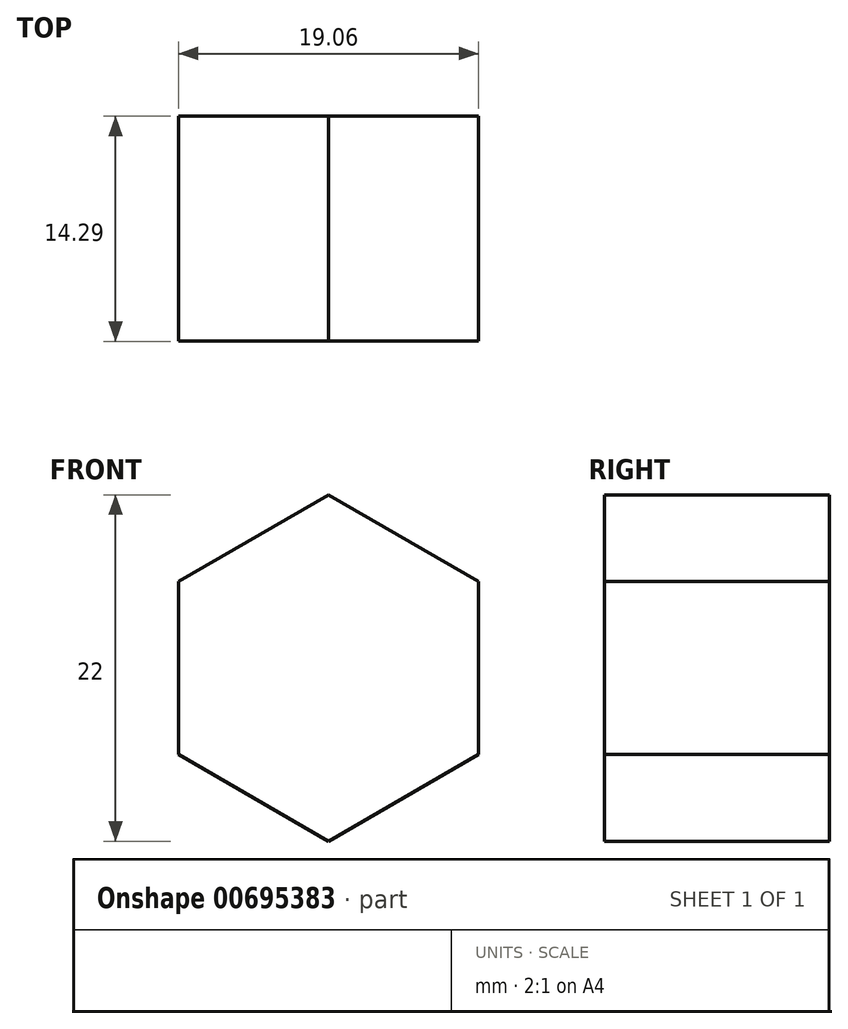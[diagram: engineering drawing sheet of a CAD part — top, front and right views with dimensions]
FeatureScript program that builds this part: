
annotation { "Feature Type Name" : "Feature", "Feature Type Description" : "" }
export const myFeature = defineFeature(function(context is Context, id is Id, definition is map)
    precondition{}
    {
        {
            var Q0;
            Q0=qCreatedBy(makeId("Front.planeOp"),FACE);
            var sketch = newSketch(context, id + "F0", { "sketchPlane" : qUnion([Q0])});
            skCircle(sketch, "E0.cCircle", {"center": v(0, 0) * mm, "radius": 9.53 * mm, "construction": true});
            skLineSegment(sketch, "E0.0", {"start": v(9.52, -5.5) * mm, "end": v(0, -11) * mm});
            skLineSegment(sketch, "E0.1", {"start": v(0, -11) * mm, "end": v(-9.53, -5.5) * mm});
            skLineSegment(sketch, "E0.2", {"start": v(-9.53, -5.5) * mm, "end": v(-9.53, 5.5) * mm});
            skLineSegment(sketch, "E0.3", {"start": v(-9.52, 5.5) * mm, "end": v(0, 11) * mm});
            skLineSegment(sketch, "E0.4", {"start": v(0, 11) * mm, "end": v(9.53, 5.5) * mm});
            skLineSegment(sketch, "E0.5", {"start": v(9.53, 5.5) * mm, "end": v(9.53, -5.5) * mm});
            skPoint(sketch, "E0.0.midPoint", {"position": v(4.76, -8.25) * mm});
            skSolve(sketch);
        }
        {
            var Q0;
            Q0 = qSketchRegion(id + "F0", true);
            extrude(context, id + "F1", {"entities" : qUnion([Q0]), "depth" : 14.29 * mm, "offsetDistance" : 25.4 * mm});
        }
    });
